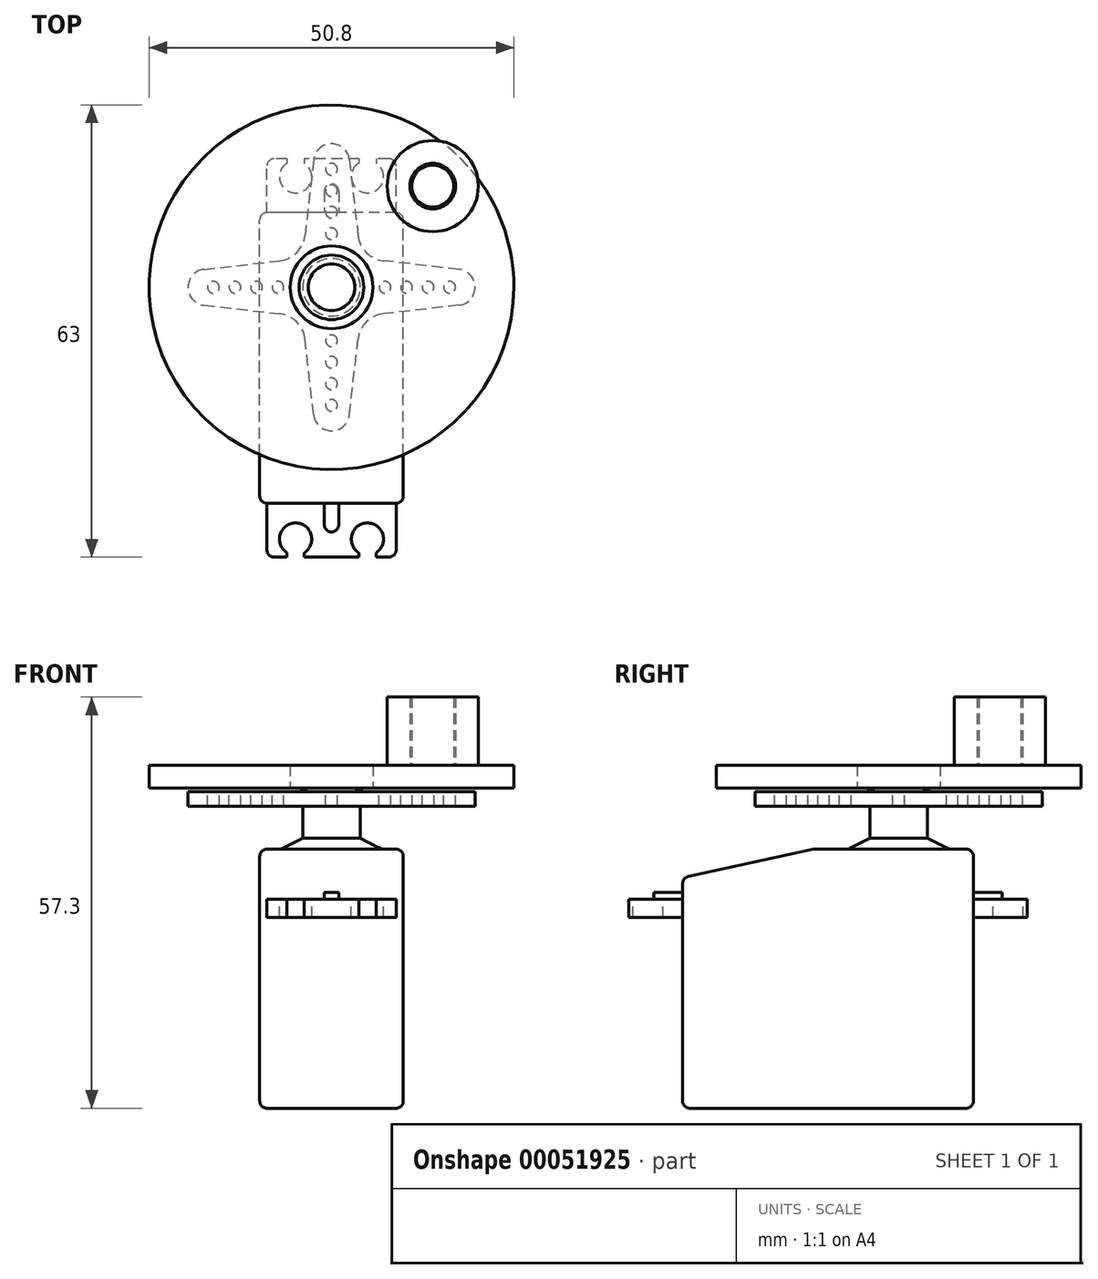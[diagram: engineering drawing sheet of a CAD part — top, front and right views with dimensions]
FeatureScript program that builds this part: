
annotation { "Feature Type Name" : "Feature", "Feature Type Description" : "" }
export const myFeature = defineFeature(function(context is Context, id is Id, definition is map)
    precondition{}
    {
        {
            var Q0;
            Q0=qCreatedBy(makeId("Right.planeOp"),FACE);
            var sketch = newSketch(context, id + "F0", { "sketchPlane" : qUnion([Q0])});
            skLineSegment(sketch, "E0.bottom", {"start": v(-20.25, 0) * mm, "end": v(20.25, 0) * mm});
            skLineSegment(sketch, "E0.top", {"start": v(-20.25, 36.1) * mm, "end": v(20.25, 36.1) * mm});
            skLineSegment(sketch, "E0.left", {"start": v(-20.25, 0) * mm, "end": v(-20.25, 36.1) * mm});
            skLineSegment(sketch, "E0.right", {"start": v(20.25, 0) * mm, "end": v(20.25, 36.1) * mm});
            skLineSegment(sketch, "E1.bottom", {"start": v(20.25, 29.1) * mm, "end": v(27.75, 29.1) * mm});
            skLineSegment(sketch, "E1.top", {"start": v(20.25, 26.6) * mm, "end": v(27.75, 26.6) * mm});
            skLineSegment(sketch, "E1.left", {"start": v(20.25, 29.1) * mm, "end": v(20.25, 26.6) * mm});
            skLineSegment(sketch, "E1.right", {"start": v(27.75, 29.1) * mm, "end": v(27.75, 26.6) * mm});
            skLineSegment(sketch, "E2.bottom", {"start": v(0, 36.1) * mm, "end": v(0, 36.1) * mm});
            skLineSegment(sketch, "E2.top", {"start": v(0, 0) * mm, "end": v(0, 0) * mm});
            skLineSegment(sketch, "E2.left", {"start": v(0, 36.1) * mm, "end": v(0, 0) * mm, "construction": true});
            skLineSegment(sketch, "E2.right", {"start": v(0, 36.1) * mm, "end": v(0, 0) * mm, "construction": true});
            skLineSegment(sketch, "E3.MirrorCS", {"start": v(-20.25, 29.1) * mm, "end": v(-27.75, 29.1) * mm});
            skLineSegment(sketch, "E4.MirrorCS", {"start": v(-27.75, 29.1) * mm, "end": v(-27.75, 26.6) * mm});
            skLineSegment(sketch, "E5.MirrorCS", {"start": v(-20.25, 26.6) * mm, "end": v(-27.75, 26.6) * mm});
            skLineSegment(sketch, "E6.MirrorCS", {"start": v(-20.25, 29.1) * mm, "end": v(-20.25, 26.6) * mm});
            skLineSegment(sketch, "E7", {"start": v(-20.25, 32.1) * mm, "end": v(-1.95, 36.1) * mm});
            skSolve(sketch);
        }
        {
            var Q0;
            {var subQ3=sQuery(id+"F0.wireOp",EDGE,"E0.bottom");Q0=makeQuery(id+"F0.imprint","IMPRINT",FACE,{"disambiguationData":[TD([[makeQuery(id+"F0.imprint","IMPRINT",EDGE,{"derivedFrom":subQ3}),1.0]])]});}
            extrude(context, id + "F1", {"entities" : qUnion([Q0]), "endBound" : BoundingType.SYMMETRIC, "depth" : 20 * mm, "hasSecondDirection" : true, "secondDirectionOppositeDirection" : true, "secondDirectionDepth" : 25 * mm});
        }
        {
            var Q0;
            Q0=makeQuery(id+"F0.imprint","IMPRINT",FACE,{"disambiguationData":[TD([[makeQuery(id+"F0.imprint","IMPRINT",EDGE,{"derivedFrom":sQuery(id+"F0.wireOp",EDGE,"E3.MirrorCS")}),1.0]])]});
            var Q1;
            Q1=makeQuery(id+"F0.imprint","IMPRINT",FACE,{"disambiguationData":[TD([[makeQuery(id+"F0.imprint","IMPRINT",EDGE,{"derivedFrom":sQuery(id+"F0.wireOp",EDGE,"E1.bottom")}),-1.0]])]});
            extrude(context, id + "F2", {"entities" : qUnion([Q0, Q1]), "operationType" : NewBodyOperationType.ADD, "endBound" : BoundingType.SYMMETRIC, "depth" : 18 * mm});
        }
        {
            var Q0;
            Q0=makeQuery(id+"F2.opExtrude","SWEPT_FACE",FACE,{"disambiguationData":[OSD([sQuery(id+"F0.wireOp",EDGE,"E3.MirrorCS")])]});
            var sketch = newSketch(context, id + "F3", { "sketchPlane" : qUnion([Q0])});
            skLineSegment(sketch, "E8.0", {"start": v(-10, -20.25) * mm, "end": v(-10, -1.95) * mm, "construction": true});
            skLineSegment(sketch, "E9.0", {"start": v(-10, -1.95) * mm, "end": v(-10, 20.25) * mm, "construction": true});
            skLineSegment(sketch, "E10.0", {"start": v(10, 20.25) * mm, "end": v(-10, 20.25) * mm, "construction": true});
            skLineSegment(sketch, "E11.0", {"start": v(10, -1.95) * mm, "end": v(10, 20.25) * mm, "construction": true});
            skLineSegment(sketch, "E12.0", {"start": v(10, -20.25) * mm, "end": v(10, -1.95) * mm, "construction": true});
            skLineSegment(sketch, "E13.0", {"start": v(10, -20.25) * mm, "end": v(-10, -20.25) * mm, "construction": true});
            skLineSegment(sketch, "E14", {"start": v(-10, -20.25) * mm, "end": v(10, 20.25) * mm, "construction": true});
            skLineSegment(sketch, "E15", {"start": v(-10, 20.25) * mm, "end": v(10, -20.25) * mm, "construction": true});
            skLineSegment(sketch, "E16", {"start": v(-10, 0) * mm, "end": v(10, 0) * mm, "construction": true});
            skPoint(sketch, "E16.endSnap0", {"position": v(0, 0) * mm});
            skLineSegment(sketch, "E17", {"start": v(0, -20.25) * mm, "end": v(0, 20.25) * mm, "construction": true});
            skCircle(sketch, "E18", {"center": v(-5, -25.25) * mm, "radius": 2.25 * mm});
            skLineSegment(sketch, "E19", {"start": v(-6.2, -27.75) * mm, "end": v(-3.8, -27.75) * mm});
            skLineSegment(sketch, "E20", {"start": v(-3.8, -27.75) * mm, "end": v(-3.8, -27.15) * mm});
            skLineSegment(sketch, "E21", {"start": v(-6.2, -27.75) * mm, "end": v(-6.2, -27.15) * mm});
            skLineSegment(sketch, "E22.MirrorCS", {"start": v(-6.2, 27.75) * mm, "end": v(-6.2, 27.15) * mm});
            skLineSegment(sketch, "E23.MirrorCS", {"start": v(-6.2, 27.75) * mm, "end": v(-3.8, 27.75) * mm});
            skLineSegment(sketch, "E24.MirrorCS", {"start": v(-3.8, 27.75) * mm, "end": v(-3.8, 27.15) * mm});
            skCircle(sketch, "E25.MirrorC", {"center": v(-5, 25.25) * mm, "radius": 2.25 * mm});
            skLineSegment(sketch, "E26.MirrorCS", {"start": v(3.8, -27.75) * mm, "end": v(3.8, -27.15) * mm});
            skLineSegment(sketch, "E27.MirrorCS", {"start": v(3.8, 27.75) * mm, "end": v(3.8, 27.15) * mm});
            skLineSegment(sketch, "E28.MirrorCS", {"start": v(6.2, 27.75) * mm, "end": v(6.2, 27.15) * mm});
            skLineSegment(sketch, "E29.MirrorCS", {"start": v(6.2, -27.75) * mm, "end": v(6.2, -27.15) * mm});
            skLineSegment(sketch, "E30.MirrorCS", {"start": v(6.2, 27.75) * mm, "end": v(3.8, 27.75) * mm});
            skLineSegment(sketch, "E31.MirrorCS", {"start": v(6.2, -27.75) * mm, "end": v(3.8, -27.75) * mm});
            skCircle(sketch, "E32.MirrorC", {"center": v(5, 25.25) * mm, "radius": 2.25 * mm});
            skCircle(sketch, "E33.MirrorC", {"center": v(5, -25.25) * mm, "radius": 2.25 * mm});
            skSolve(sketch);
        }
        {
            var Q0;
            Q0=qSketchRegion(id+"F3",true);
            extrude(context, id + "F4", {"entities" : qUnion([Q0]), "operationType" : NewBodyOperationType.REMOVE, "oppositeDirection" : true, "depth" : 25 * mm});
        }
        {
            var Q0;
            Q0=makeQuery(id+"F2.opExtrude","SWEPT_FACE",FACE,{"disambiguationData":[OSD([sQuery(id+"F0.wireOp",EDGE,"E3.MirrorCS")])]});
            var sketch = newSketch(context, id + "F5", { "sketchPlane" : qUnion([Q0])});
            skLineSegment(sketch, "E34.0", {"start": v(10, -20.25) * mm, "end": v(-10, -20.25) * mm, "construction": true});
            skLineSegment(sketch, "E35.0", {"start": v(10, 20.25) * mm, "end": v(-10, 20.25) * mm, "construction": true});
            skLineSegment(sketch, "E36", {"start": v(0, -20.25) * mm, "end": v(0, 20.25) * mm, "construction": true});
            skLineSegment(sketch, "E37.rect.bottom", {"start": v(1, 23.25) * mm, "end": v(-1, 23.25) * mm});
            skLineSegment(sketch, "E37.rect.top", {"start": v(1, -23.25) * mm, "end": v(-1, -23.25) * mm});
            skLineSegment(sketch, "E37.rect.left", {"start": v(1, 23.25) * mm, "end": v(1, -23.25) * mm});
            skLineSegment(sketch, "E37.rect.right", {"start": v(-1, 23.25) * mm, "end": v(-1, -23.25) * mm});
            skPoint(sketch, "E37.rect.middle", {"position": v(0, 0) * mm});
            skArc(sketch, "E38", {"start": v(1, 23.25) * mm, "mid": v(0, 24.25) * mm, "end": v(-1, 23.25) * mm});
            skArc(sketch, "E39", {"start": v(-1, -23.25) * mm, "mid": v(0, -24.25) * mm, "end": v(1, -23.25) * mm});
            skPoint(sketch, "E40", {"position": v(0, 24.25) * mm});
            skSolve(sketch);
        }
        {
            var Q0;
            Q0=qSketchRegion(id+"F5",true);
            extrude(context, id + "F6", {"entities" : qUnion([Q0]), "operationType" : NewBodyOperationType.ADD, "depth" : 1 * mm});
        }
        {
            var Q0;
            Q0=qCreatedBy(makeId("Right.planeOp"),FACE);
            var sketch = newSketch(context, id + "F7", { "sketchPlane" : qUnion([Q0])});
            skLineSegment(sketch, "E41.0", {"start": v(-1.95, 36.1) * mm, "end": v(20.25, 36.1) * mm, "construction": true});
            skLineSegment(sketch, "E42.0", {"start": v(-20.25, 0) * mm, "end": v(-20.25, 32.1) * mm, "construction": true});
            skLineSegment(sketch, "E43.0", {"start": v(20.25, 0) * mm, "end": v(20.25, 36.1) * mm, "construction": true});
            skLineSegment(sketch, "E44", {"start": v(9.85, 53.58) * mm, "end": v(9.85, 24.34) * mm, "construction": true});
            skLineSegment(sketch, "E45", {"start": v(16.85, 36.1) * mm, "end": v(13.85, 37.6) * mm});
            skLineSegment(sketch, "E46", {"start": v(13.85, 37.6) * mm, "end": v(13.85, 42.1) * mm});
            skLineSegment(sketch, "E47", {"start": v(13.85, 42.1) * mm, "end": v(29.85, 42.1) * mm});
            skLineSegment(sketch, "E48", {"start": v(29.85, 42.1) * mm, "end": v(29.85, 44.1) * mm});
            skLineSegment(sketch, "E49", {"start": v(29.85, 44.1) * mm, "end": v(14.35, 44.1) * mm});
            skLineSegment(sketch, "E50", {"start": v(14.35, 44.1) * mm, "end": v(13.1, 44.6) * mm});
            skLineSegment(sketch, "E51", {"start": v(13.1, 44.6) * mm, "end": v(9.85, 44.6) * mm});
            skLineSegment(sketch, "E52", {"start": v(9.85, 44.6) * mm, "end": v(9.85, 36.1) * mm});
            skLineSegment(sketch, "E53", {"start": v(9.85, 36.1) * mm, "end": v(16.85, 36.1) * mm});
            skSolve(sketch);
        }
        {
            var Q0;
            Q0=qSketchRegion(id+"F7",true);
            var Q1;
            Q1=sQuery(id+"F7.wireOp",EDGE,"E44");
            revolve(context, id + "F8", {"operationType" : NewBodyOperationType.ADD, "entities" : qUnion([Q0]), "axis" : qUnion([Q1]), "revolveType" : RevolveType.FULL});
        }
        {
            var Q0;
            Q0=makeQuery(id+"F8.opRevolve","SWEPT_FACE",FACE,{"disambiguationData":[OSD([sQuery(id+"F7.wireOp",EDGE,"E49")])]});
            var sketch = newSketch(context, id + "F9", { "sketchPlane" : qUnion([Q0])});
            skPoint(sketch, "E54", {"position": v(0, 9.85) * mm});
            skCircle(sketch, "E55", {"center": v(0, 17.3) * mm, "radius": 0.81 * mm});
            skCircle(sketch, "E56", {"center": v(0, 20.3) * mm, "radius": 0.81 * mm});
            skCircle(sketch, "E57", {"center": v(0, 23.3) * mm, "radius": 0.81 * mm});
            skCircle(sketch, "E58", {"center": v(0, 26.3) * mm, "radius": 0.81 * mm});
            skCircle(sketch, "E59.1.0", {"center": v(-16.45, 9.85) * mm, "radius": 0.81 * mm});
            skCircle(sketch, "E59.1.1", {"center": v(-13.45, 9.85) * mm, "radius": 0.81 * mm});
            skCircle(sketch, "E59.1.2", {"center": v(-10.45, 9.85) * mm, "radius": 0.81 * mm});
            skCircle(sketch, "E59.1.3", {"center": v(-7.45, 9.85) * mm, "radius": 0.81 * mm});
            skCircle(sketch, "E59.2.0", {"center": v(0, -6.6) * mm, "radius": 0.81 * mm});
            skCircle(sketch, "E59.2.1", {"center": v(0, -3.6) * mm, "radius": 0.81 * mm});
            skCircle(sketch, "E59.2.2", {"center": v(0, -0.6) * mm, "radius": 0.81 * mm});
            skCircle(sketch, "E59.2.3", {"center": v(0, 2.4) * mm, "radius": 0.81 * mm});
            skCircle(sketch, "E59.3.0", {"center": v(16.45, 9.85) * mm, "radius": 0.81 * mm});
            skCircle(sketch, "E59.3.1", {"center": v(13.45, 9.85) * mm, "radius": 0.81 * mm});
            skCircle(sketch, "E59.3.2", {"center": v(10.45, 9.85) * mm, "radius": 0.81 * mm});
            skCircle(sketch, "E59.3.3", {"center": v(7.45, 9.85) * mm, "radius": 0.81 * mm});
            skSolve(sketch);
        }
        {
            var Q0;
            Q0=qSketchRegion(id+"F9",true);
            extrude(context, id + "F10", {"entities" : qUnion([Q0]), "operationType" : NewBodyOperationType.REMOVE, "endBound" : BoundingType.UP_TO_NEXT, "oppositeDirection" : true, "depth" : 25 * mm});
        }
        {
            var Q0;
            Q0=makeQuery(id+"F8.opRevolve","SWEPT_FACE",FACE,{"disambiguationData":[OSD([sQuery(id+"F7.wireOp",EDGE,"E49")])]});
            var sketch = newSketch(context, id + "F11", { "sketchPlane" : qUnion([Q0])});
            skPoint(sketch, "E60", {"position": v(0, 9.85) * mm});
            skLineSegment(sketch, "E61", {"start": v(0, 9.85) * mm, "end": v(0, 29.85) * mm, "construction": true});
            skLineSegment(sketch, "E62", {"start": v(0, 9.85) * mm, "end": v(-14.14, 24) * mm, "construction": true});
            skLineSegment(sketch, "E63", {"start": v(0, 9.85) * mm, "end": v(14.14, 24) * mm, "construction": true});
            skLineSegment(sketch, "E64", {"start": v(-3.69, 17.1) * mm, "end": v(-2.5, 27.62) * mm});
            skArc(sketch, "E65", {"start": v(0, 29.85) * mm, "mid": v(-1.68, 29.21) * mm, "end": v(-2.5, 27.62) * mm});
            skArc(sketch, "E66", {"start": v(-4.84, 14.7) * mm, "mid": v(-4.06, 15.8) * mm, "end": v(-3.69, 17.1) * mm});
            skArc(sketch, "E67.MirrorCS", {"start": v(4.84, 14.7) * mm, "mid": v(4.06, 15.8) * mm, "end": v(3.69, 17.1) * mm});
            skLineSegment(sketch, "E68.MirrorCS", {"start": v(3.69, 17.1) * mm, "end": v(2.5, 27.62) * mm});
            skArc(sketch, "E69.MirrorCS", {"start": v(0, 29.85) * mm, "mid": v(1.68, 29.21) * mm, "end": v(2.5, 27.62) * mm});
            skArc(sketch, "E70.1.0", {"start": v(-4.84, 5) * mm, "mid": v(-5.95, 5.79) * mm, "end": v(-7.24, 6.16) * mm});
            skLineSegment(sketch, "E70.1.1", {"start": v(-7.24, 6.16) * mm, "end": v(-17.77, 7.35) * mm});
            skArc(sketch, "E70.1.2", {"start": v(-20, 9.85) * mm, "mid": v(-19.36, 8.17) * mm, "end": v(-17.77, 7.35) * mm});
            skArc(sketch, "E70.1.3", {"start": v(-20, 9.85) * mm, "mid": v(-19.36, 11.53) * mm, "end": v(-17.77, 12.35) * mm});
            skLineSegment(sketch, "E70.1.4", {"start": v(-7.24, 13.54) * mm, "end": v(-17.77, 12.35) * mm});
            skArc(sketch, "E70.1.5", {"start": v(-4.84, 14.7) * mm, "mid": v(-5.95, 13.91) * mm, "end": v(-7.24, 13.54) * mm});
            skArc(sketch, "E70.2.0", {"start": v(4.84, 5) * mm, "mid": v(4.06, 3.9) * mm, "end": v(3.69, 2.6) * mm});
            skLineSegment(sketch, "E70.2.1", {"start": v(3.69, 2.6) * mm, "end": v(2.5, -7.92) * mm});
            skArc(sketch, "E70.2.2", {"start": v(0, -10.15) * mm, "mid": v(1.68, -9.51) * mm, "end": v(2.5, -7.92) * mm});
            skArc(sketch, "E70.2.3", {"start": v(0, -10.15) * mm, "mid": v(-1.68, -9.51) * mm, "end": v(-2.5, -7.92) * mm});
            skLineSegment(sketch, "E70.2.4", {"start": v(-3.69, 2.6) * mm, "end": v(-2.5, -7.92) * mm});
            skArc(sketch, "E70.2.5", {"start": v(-4.84, 5) * mm, "mid": v(-4.06, 3.9) * mm, "end": v(-3.69, 2.6) * mm});
            skArc(sketch, "E70.3.0", {"start": v(4.84, 14.7) * mm, "mid": v(5.95, 13.91) * mm, "end": v(7.24, 13.54) * mm});
            skLineSegment(sketch, "E70.3.1", {"start": v(7.24, 13.54) * mm, "end": v(17.77, 12.35) * mm});
            skArc(sketch, "E70.3.2", {"start": v(20, 9.85) * mm, "mid": v(19.36, 11.53) * mm, "end": v(17.77, 12.35) * mm});
            skArc(sketch, "E70.3.3", {"start": v(20, 9.85) * mm, "mid": v(19.36, 8.17) * mm, "end": v(17.77, 7.35) * mm});
            skLineSegment(sketch, "E70.3.4", {"start": v(7.24, 6.16) * mm, "end": v(17.77, 7.35) * mm});
            skArc(sketch, "E70.3.5", {"start": v(4.84, 5) * mm, "mid": v(5.95, 5.79) * mm, "end": v(7.24, 6.16) * mm});
            skCircle(sketch, "E71", {"center": v(0, 9.85) * mm, "radius": 26.3 * mm});
            skSolve(sketch);
        }
        {
            var Q0;
            Q0=qSketchRegion(id+"F11",true);
            var Q1;
            Q1=makeQuery(id+"F8.opRevolve","SWEPT_FACE",FACE,{"disambiguationData":[OSD([sQuery(id+"F7.wireOp",EDGE,"E47")])]});
            extrude(context, id + "F12", {"entities" : qUnion([Q0]), "operationType" : NewBodyOperationType.REMOVE, "endBound" : BoundingType.UP_TO_SURFACE, "oppositeDirection" : true, "endBoundEntityFace" : qUnion([Q1]), "depth" : 25 * mm});
        }
        {
            var Q0;
            Q0=makeQuery(id+"F1.opExtrude","CAP_FACE",FACE,{"disambiguationData":[OSD([sQuery(id+"F0.wireOp",EDGE,"E0.bottom"),sQuery(id+"F0.wireOp",EDGE,"E0.top"),sQuery(id+"F0.wireOp",EDGE,"E0.left"),sQuery(id+"F0.wireOp",EDGE,"E0.right"),sQuery(id+"F0.wireOp",EDGE,"E1.left"),sQuery(id+"F0.wireOp",EDGE,"E6.MirrorCS"),sQuery(id+"F0.wireOp",EDGE,"E7")])],"isStart":false});
            var Q1;
            Q1=makeQuery(id+"F1.opExtrude","CAP_FACE",FACE,{"disambiguationData":[OSD([sQuery(id+"F0.wireOp",EDGE,"E0.bottom"),sQuery(id+"F0.wireOp",EDGE,"E0.top"),sQuery(id+"F0.wireOp",EDGE,"E0.left"),sQuery(id+"F0.wireOp",EDGE,"E0.right"),sQuery(id+"F0.wireOp",EDGE,"E1.left"),sQuery(id+"F0.wireOp",EDGE,"E6.MirrorCS"),sQuery(id+"F0.wireOp",EDGE,"E7")])],"isStart":true});
            var Q2;
            Q2=makeQuery(id+"F1.opExtrude","SWEPT_FACE",FACE,{"disambiguationData":[OSD([sQuery(id+"F0.wireOp",EDGE,"E0.bottom")])]});
            var Q3;
            Q3=makeQuery(id+"F1.opExtrude","SWEPT_FACE",FACE,{"disambiguationData":[OSD([sQuery(id+"F0.wireOp",EDGE,"E7")])]});
            var Q4;
            Q4=makeQuery(id+"F1.opExtrude","SWEPT_FACE",FACE,{"disambiguationData":[OSD([sQuery(id+"F0.wireOp",EDGE,"E0.top")])]});
            var Q5;
            Q5=makeQuery(id+"F2.opExtrude","CAP_EDGE",EDGE,{"disambiguationData":[OSD([sQuery(id+"F0.wireOp",EDGE,"E4.MirrorCS")])],"isStart":false});
            var Q6;
            Q6=makeQuery(id+"F2.opExtrude","CAP_EDGE",EDGE,{"disambiguationData":[OSD([sQuery(id+"F0.wireOp",EDGE,"E4.MirrorCS")])],"isStart":true});
            var Q7;
            Q7=makeQuery(id+"F2.opExtrude","CAP_EDGE",EDGE,{"disambiguationData":[OSD([sQuery(id+"F0.wireOp",EDGE,"E1.right")])],"isStart":false});
            var Q8;
            Q8=makeQuery(id+"F2.opExtrude","CAP_EDGE",EDGE,{"disambiguationData":[OSD([sQuery(id+"F0.wireOp",EDGE,"E1.right")])],"isStart":true});
            fillet(context, id + "F13", {"entities" : qUnion([Q0, Q1, Q2, Q3, Q4, Q5, Q6, Q7, Q8]), "radius" : 1 * mm, "tangentPropagation" : true, "allowEdgeOverflow" : false});
        }
        {
            var Q0;
            Q0=makeQuery(id+"F8.opRevolve","SWEPT_FACE",FACE,{"disambiguationData":[OSD([sQuery(id+"F7.wireOp",EDGE,"E51")])]});
            var sketch = newSketch(context, id + "F14", { "sketchPlane" : qUnion([Q0])});
            skCircle(sketch, "E72", {"center": v(0, 9.85) * mm, "radius": 25.4 * mm});
            skCircle(sketch, "E73.0", {"center": v(0, 9.85) * mm, "radius": 4.5 * mm, "construction": true});
            skCircle(sketch, "E74.0", {"center": v(0, 9.85) * mm, "radius": 5.77 * mm});
            skSolve(sketch);
        }
        {
            var Q0;
            Q0=makeQuery(id+"F14.imprint","IMPRINT",FACE,{"disambiguationData":[TD([[makeQuery(id+"F14.imprint","IMPRINT",EDGE,{"derivedFrom":sQuery(id+"F14.wireOp",EDGE,"E72")}),1.0]])]});
            extrude(context, id + "F15", {"entities" : qUnion([Q0]), "depth" : 3.17 * mm});
        }
        {
            var Q0;
            Q0=makeQuery(id+"F15.opExtrude","CAP_FACE",FACE,{"disambiguationData":[OSD([sQuery(id+"F14.wireOp",EDGE,"E72"),sQuery(id+"F14.wireOp",EDGE,"E74.0")])],"isStart":false});
            var sketch = newSketch(context, id + "F16", { "sketchPlane" : qUnion([Q0])});
            skCircle(sketch, "E75", {"center": v(14.1, 23.95) * mm, "radius": 2.92 * mm});
            skPoint(sketch, "E76", {"position": v(0, 9.85) * mm});
            skLineSegment(sketch, "E77", {"start": v(0, 9.85) * mm, "end": v(14.1, 23.95) * mm, "construction": true});
            skLineSegment(sketch, "E78", {"start": v(0.52, 9.85) * mm, "end": v(25.4, 9.85) * mm, "construction": true});
            skLineSegment(sketch, "E79", {"start": v(14.1, 23.95) * mm, "end": v(16.16, 26.01) * mm, "construction": true});
            skSolve(sketch);
        }
        {
            var Q0;
            Q0=makeQuery(id+"F16.imprint","IMPRINT",FACE,{"disambiguationData":[TD([[makeQuery(id+"F16.imprint","IMPRINT",EDGE,{"derivedFrom":sQuery(id+"F16.wireOp",EDGE,"E75")}),1.0]])]});
            extrude(context, id + "F17", {"entities" : qUnion([Q0]), "operationType" : NewBodyOperationType.ADD, "depth" : 9.52 * mm});
        }
        {
            var Q0;
            Q0=makeQuery(id+"F15.opExtrude","CAP_FACE",FACE,{"disambiguationData":[OSD([sQuery(id+"F14.wireOp",EDGE,"E72"),sQuery(id+"F14.wireOp",EDGE,"E74.0")])],"isStart":false});
            var sketch = newSketch(context, id + "F18", { "sketchPlane" : qUnion([Q0])});
            skCircle(sketch, "E80.0", {"center": v(14.1, 23.95) * mm, "radius": 2.92 * mm, "construction": true});
            skCircle(sketch, "E81", {"center": v(14.1, 23.95) * mm, "radius": 6.35 * mm});
            skCircle(sketch, "E82.0", {"center": v(14.1, 23.95) * mm, "radius": 3.18 * mm});
            skSolve(sketch);
        }
        {
            var Q0;
            Q0=makeQuery(id+"F18.imprint","IMPRINT",FACE,{"disambiguationData":[TD([[makeQuery(id+"F18.imprint","IMPRINT",EDGE,{"derivedFrom":sQuery(id+"F18.wireOp",EDGE,"E80.0")}),-1.0]])]});
            var Q1;
            {var subQ0=sQuery(id+"F18.wireOp",EDGE,"E81");var subQ1=makeQuery(id+"F15.opExtrude","CAP_EDGE",EDGE,{"disambiguationData":[OSD([sQuery(id+"F14.wireOp",EDGE,"E72")])],"isStart":false});var subQ2=makeQuery(id+"F18.imprint","INTERSECT",VERTEX,{"disambiguationData":[OD(0.0)],"derivedFrom":[subQ1,subQ0]});Q1=makeQuery(id+"F18.imprint","IMPRINT",FACE,{"disambiguationData":[TD([[makeQuery(id+"F18.imprint","IMPRINT",EDGE,{"disambiguationData":[TD([[subQ2,1.0]])],"derivedFrom":subQ0}),1.0]])]});}
            var Q2;
            Q2=makeQuery(id+"F18.imprint","IMPRINT",FACE,{"disambiguationData":[TD([[makeQuery(id+"F18.imprint","IMPRINT",EDGE,{"derivedFrom":sQuery(id+"F18.wireOp",EDGE,"E82.0")}),-1.0]])]});
            extrude(context, id + "F19", {"entities" : qUnion([Q0, Q1, Q2]), "depth" : 9.52 * mm});
        }
    });
